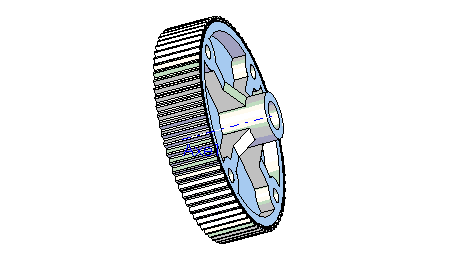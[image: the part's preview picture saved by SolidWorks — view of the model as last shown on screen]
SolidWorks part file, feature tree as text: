
SOLIDWORKS PART (.sldprt)
format: sldprt  version: not decoded by parser v0  size: 1,018,368 bytes
history: native  units: mm
features: sketch x10, extrude x5, plane x3, fillet x3, pattern_circular x3, material x1, cut_extrude x1, hole x1 + 1 further entry (+7 scaffold rows collapsed)
feature tree (35):
  scaffold x7  (default folders/planes/origin — collapsed)
  material  "Matériau <non spécifié>"
  "Corps de surface"
  plane  "Face"
  plane  "Dessus"
  plane  "Droite"
  sketch  "Esquisse1"  dims[D1=45.0mm D2=6.0mm]
  extrude  "Extrusion1"  Depth=10mm
  sketch  "Esquisse2"  dims[c1.D1=43.0mm c1.D6=45.0mm c1.D2=~39.33126mm c2.D2=0.5deg c2.D3=~33.470119mm c3.D3=0.5deg c3.D4=~37.160012mm c4.D4=4.08deg c4.D5=~39.034362mm c5.D5=2.54deg]
  cut_extrude  "Enlèv. mat.-Extru.1"  [1 undecoded]
  fillet  "Congé1"  Radius=0.25mm
  pattern_circular  "Répétition circulaire2"  Count=71 Angle=5.070423deg
  sketch  "Esquisse3"  dims[c1.D2=19.0mm c1.D3=37.0mm c1.D6=8.0mm c1.D7=8.0mm c1.D1=~18.429632mm c2.D1=90.0deg c2.D4=1.5mm c2.D5=1.5mm]
  fillet  "Enlèv. mat.-Extru.2"  Radius=3mm
  pattern_circular  "Répétition circulaire3"  Count=4 Angle=90deg
  hole  "Diamètre du perçage M3.0 (3.000000)1"  Diameter=3mm Depth=10mm
  sketch  "Esquisse6"
  sketch  "Esquisse5"  dims[hole-wizard template sketch: 46 standard entries collapsed; hole parameters kept: c15.Diamètre du perçage=3.0mm c15.Profondeur du perçage=10.0mm c15.D3=~14.816244mm c15.Angle de pointe=118.0deg]
  sketch  "Esquisse7"  dims[D1=19.0mm D2=6.0mm D3=14.0mm D4=10.0mm D5=2.0mm D6=3.0mm D7=3.0mm]
  extrude  "Extrusion2"  Depth=3mm
  sketch  "Esquisse8"  dims[D1=10.0mm D2=39.0mm D3=8.0mm D4=1.5mm D5=1.5mm]
  fillet  "Enlèv. mat.-Extru.3"  Radius=3mm
  sketch  "Esquisse9"
  extrude  "Extrusion3"  Depth=7mm
  sketch  "Esquisse11"  dims[c1.D1=5.0mm c1.D2=~5.774051mm c2.D2=30.0deg]
  extrude  "Extrusion4"  Depth=3mm
  pattern_circular  "Répétition circulaire4"  Count=4 Angle=90deg
  sketch  "Esquisse12"  dims[D1=44.0mm D2=43.0mm]
  extrude  "Extrusion5"  Depth=0.1mm
decode coverage: 20 of 23 modeling features carry decoded parameters; 1 rows unclassified (native names shown)
note: ~ marks probable driven/reference dimensions
note: 1 parameter value undecoded
note: suppression state not decoded; provenance and decode notes live in map.json
